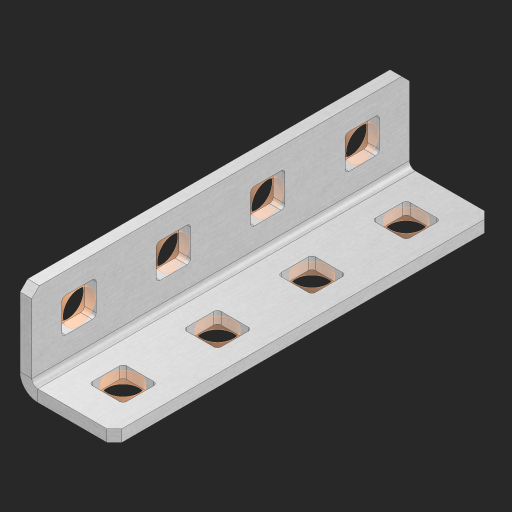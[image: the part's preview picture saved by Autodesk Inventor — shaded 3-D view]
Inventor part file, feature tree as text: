
AUTODESK INVENTOR PART (.ipt)
format: ipt  version: 2023 (Build 270158000, 158)  size: 487,424 bytes
history: native  units: in
note: dims shown in document units (in); Inventor stores cm internally (conversion verified against a paired STEP export)
features: other x14, extrude x9, sheet_metal_op x8, sketch x5, pattern_linear x1, mirror x1, chamfer x1
ambient origin geometry x8: Origin, YZ Plane, XZ Plane, XY Plane, X Axis, Y Axis, Z Axis, Center Point
bodies: Solid1 (feature_tree), Body (feature_tree)
feature tree (39):
  sheet_metal_op  "Flanges"
  sheet_metal_op  "Body Pattern"
  other  "Arc Length"
  pattern_linear  "Notch Pattern"  Spacing1=0.125in  [1 undecoded]
  other  "Diagonal Plane"
  mirror  "Everything Mirrored"
  chamfer  "End Chamfer"
  sketch  "Sketch1"  dims[d0=0.5in]
  other  "Plate1"
  sketch  "Sketch2"  dims[d1=2.0in]
  other  "Plate2"
  sheet_metal_op  "Bend1"
  sheet_metal_op  "Corner1"
  sketch  "Sketch8"  dims[d2=0.0625in]
  sketch  "Sketch9"  dims[d3=0.0625in]
  other  "Srf91"
  sheet_metal_op  "Body Pattern Sketch"
  other  "Srf92"
  sketch  "Sketch13"  dims[d4=0.0312in d5=0.125in d6=0.0625in d7=0.5in d8=90.0deg d9=0.0312in d10=0.25in d11=0.0625in d12=0.0625in d49=0.182in d50=0.02in d52=0.25in d53=0.0625in d54=0.0in d55=0.172in d56=1.0in d57=0.0in d85=0.1473in d86=0.1782in d89=0.0625in d90=0.0in d91=0.04in d92=0.0491in d95=2.5in d96=0.04in d97=0.25in d98=45.0deg d123=0.204in d126=0.0491in d127=0.1473in d128=0.08in d129=0.04in d130=2.5in d131=1.5748in d133=0.5in d134=0.3937in d136=1.0in]
  other  "Srf856"
  other  "Srf857"
  other  "Srf858"
  other  "Srf1275"
  other  "Srf1276"
  other  "Srf1278"
  other  "Srf1279"
  other  "Srf1280"
  sheet_metal_op  "Body Stamp"
  sheet_metal_op  "Body Circle"
  sheet_metal_op  "Notch"
  extrude  "ExtrusionSrf92"  Depth=0.0625in
  extrude  "ExtrusionSrf856"  Depth=0.5in TaperAngle=90.0deg
  extrude  "ExtrusionSrf857"  Depth=0.25in
  extrude  "ExtrusionSrf858"  Depth=0.0625in
  extrude  "ExtrusionSrf1275"  Depth=0.0625in
  extrude  "ExtrusionSrf1276"  Depth=0.182in
  extrude  "ExtrusionSrf1277"  Depth=0.02in
  extrude  "ExtrusionSrf1278"  Depth=0.25in
  extrude  "ExtrusionSrf1279"  Depth=0.0625in
note: 1 required parameter value undecoded (feature->parameter linkage not recoverable at this tier; creation-order binding heuristic only, values carry confidence <= 0.55)
